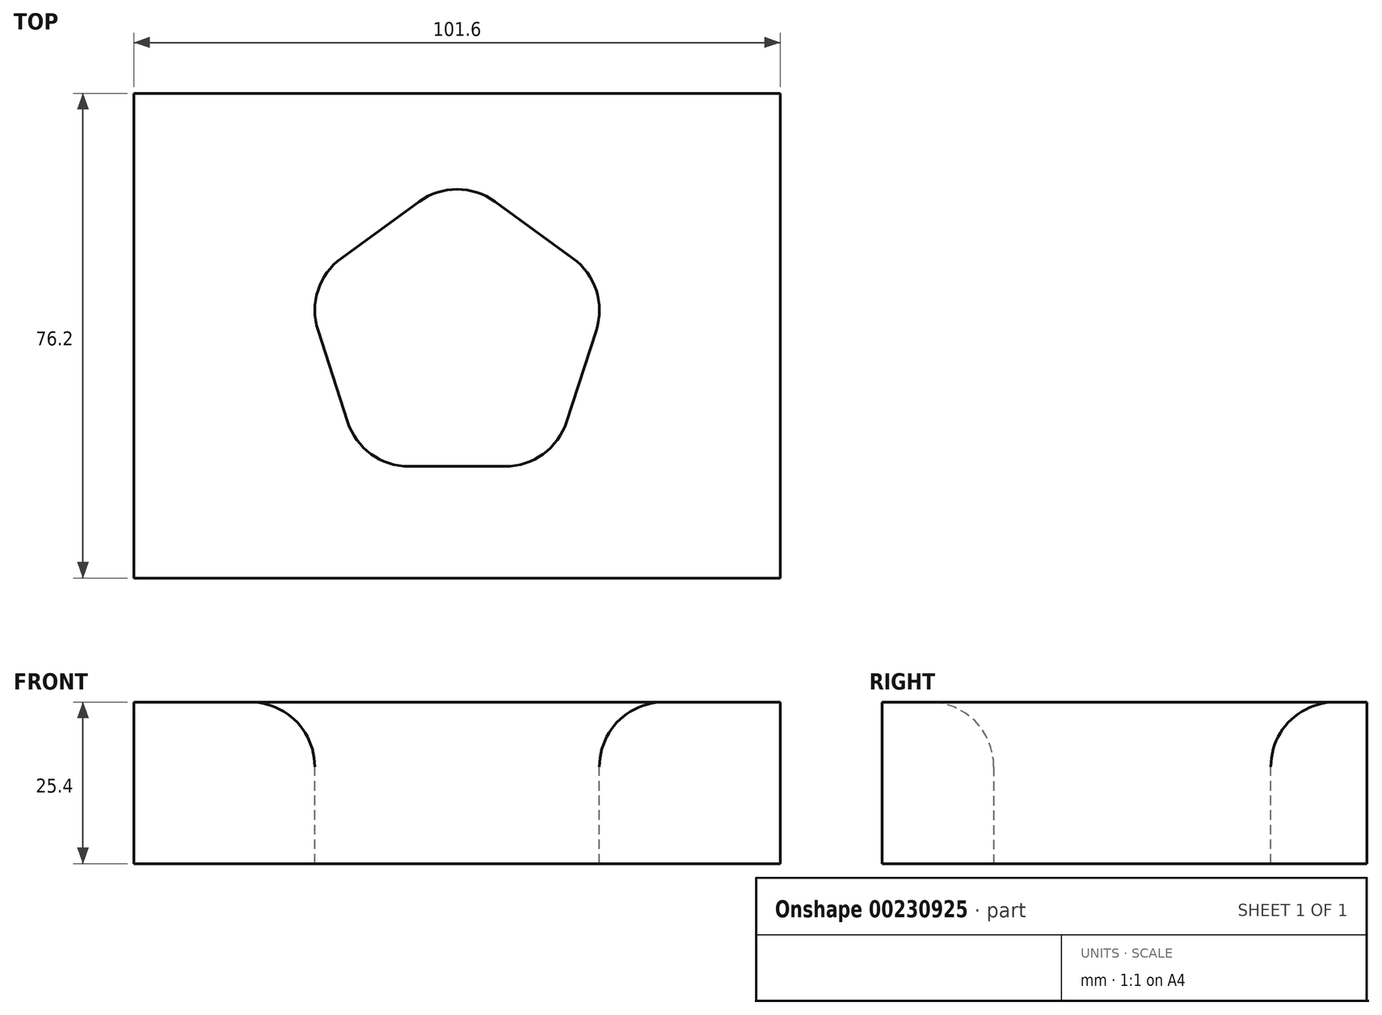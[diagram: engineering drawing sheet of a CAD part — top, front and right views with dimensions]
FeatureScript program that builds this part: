
annotation { "Feature Type Name" : "Feature", "Feature Type Description" : "" }
export const myFeature = defineFeature(function(context is Context, id is Id, definition is map)
    precondition{}
    {
        {
            var Q0;
            Q0=qCreatedBy(makeId("Top.planeOp"),FACE);
            var sketch = newSketch(context, id + "F0", { "sketchPlane" : qUnion([Q0])});
            skLineSegment(sketch, "E0.bottom", {"start": v(-50.8, 38.1) * mm, "end": v(50.8, 38.1) * mm});
            skLineSegment(sketch, "E0.top", {"start": v(-50.8, -38.1) * mm, "end": v(50.8, -38.1) * mm});
            skLineSegment(sketch, "E0.left", {"start": v(-50.8, 38.1) * mm, "end": v(-50.8, -38.1) * mm});
            skLineSegment(sketch, "E0.right", {"start": v(50.8, 38.1) * mm, "end": v(50.8, -38.1) * mm});
            skPoint(sketch, "E0.middle", {"position": v(0, 0) * mm});
            skCircle(sketch, "E1.cCircle", {"center": v(0, 0) * mm, "radius": 25.4 * mm, "construction": true});
            skLineSegment(sketch, "E1.0", {"start": v(0, 25.4) * mm, "end": v(24.16, 7.85) * mm});
            skLineSegment(sketch, "E1.1", {"start": v(24.16, 7.85) * mm, "end": v(14.93, -20.55) * mm});
            skLineSegment(sketch, "E1.2", {"start": v(14.93, -20.55) * mm, "end": v(-14.93, -20.55) * mm});
            skLineSegment(sketch, "E1.3", {"start": v(-14.93, -20.55) * mm, "end": v(-24.16, 7.85) * mm});
            skLineSegment(sketch, "E1.4", {"start": v(-24.16, 7.85) * mm, "end": v(0, 25.4) * mm});
            skSolve(sketch);
        }
        {
            var Q0;
            Q0 = qSketchRegion(id + "F0", true);
            extrude(context, id + "F1", {"entities" : qUnion([Q0]), "depth" : 25.4 * mm});
        }
        {
            var Q0;
            Q0=makeQuery(id+"F1.opExtrude","CAP_EDGE",EDGE,{"disambiguationData":[OSD([sQuery(id+"F0.wireOp",EDGE,"E1.2")])],"isStart":false});
            var Q1;
            Q1=makeQuery(id+"F1.opExtrude","CAP_EDGE",EDGE,{"disambiguationData":[OSD([sQuery(id+"F0.wireOp",EDGE,"E1.3")])],"isStart":false});
            var Q2;
            Q2=makeQuery(id+"F1.opExtrude","CAP_EDGE",EDGE,{"disambiguationData":[OSD([sQuery(id+"F0.wireOp",EDGE,"E1.4")])],"isStart":false});
            var Q3;
            Q3=makeQuery(id+"F1.opExtrude","CAP_EDGE",EDGE,{"disambiguationData":[OSD([sQuery(id+"F0.wireOp",EDGE,"E1.0")])],"isStart":false});
            var Q4;
            Q4=makeQuery(id+"F1.opExtrude","CAP_EDGE",EDGE,{"disambiguationData":[OSD([sQuery(id+"F0.wireOp",EDGE,"E1.1")])],"isStart":false});
            var Q5;
            Q5=makeQuery(id+"F1.opExtrude","SWEPT_EDGE",EDGE,{"disambiguationData":[OSD([sQuery(id+"F0.wireOp",EDGE,"E1.2"),sQuery(id+"F0.wireOp",EDGE,"E1.3")])]});
            var Q6;
            Q6=makeQuery(id+"F1.opExtrude","SWEPT_EDGE",EDGE,{"disambiguationData":[OSD([sQuery(id+"F0.wireOp",EDGE,"E1.1"),sQuery(id+"F0.wireOp",EDGE,"E1.2")])]});
            var Q7;
            Q7=makeQuery(id+"F1.opExtrude","SWEPT_EDGE",EDGE,{"disambiguationData":[OSD([sQuery(id+"F0.wireOp",EDGE,"E1.0"),sQuery(id+"F0.wireOp",EDGE,"E1.1")])]});
            var Q8;
            Q8=makeQuery(id+"F1.opExtrude","SWEPT_EDGE",EDGE,{"disambiguationData":[OSD([sQuery(id+"F0.wireOp",EDGE,"E1.0"),sQuery(id+"F0.wireOp",EDGE,"E1.4")])]});
            var Q9;
            Q9=makeQuery(id+"F1.opExtrude","SWEPT_EDGE",EDGE,{"disambiguationData":[OSD([sQuery(id+"F0.wireOp",EDGE,"E1.3"),sQuery(id+"F0.wireOp",EDGE,"E1.4")])]});
            fillet(context, id + "F2", {"entities" : qUnion([Q0, Q1, Q2, Q3, Q4, Q5, Q6, Q7, Q8, Q9]), "radius" : 10.16 * mm, "tangentPropagation" : true, "allowEdgeOverflow" : false});
        }
    });
